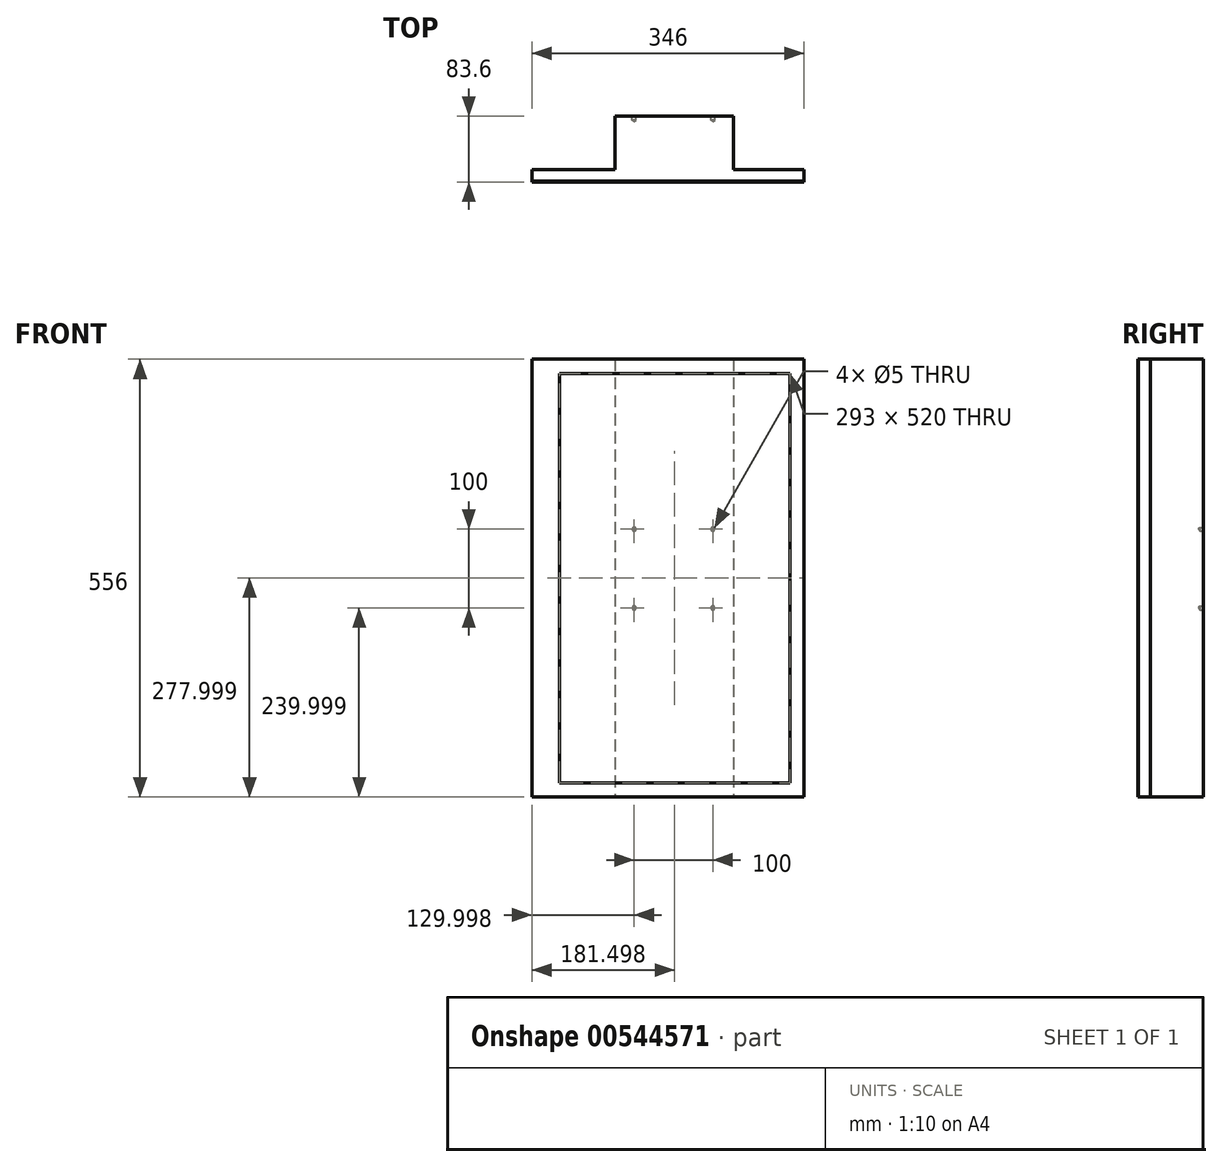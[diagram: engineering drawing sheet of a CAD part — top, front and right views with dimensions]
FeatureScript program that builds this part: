
annotation { "Feature Type Name" : "Feature", "Feature Type Description" : "" }
export const myFeature = defineFeature(function(context is Context, id is Id, definition is map)
    precondition{}
    {
        {
            assignVariable(context, id + "F0", {"name" : "mindepth", "anyValue" : 15});
        }
        {
            assignVariable(context, id + "F1", {"name" : "maxdepth", "anyValue" : 67.6});
        }
        {
            var Q0;
            Q0=qCreatedBy(makeId("Front.planeOp"),FACE);
            var sketch = newSketch(context, id + "F2", { "sketchPlane" : qUnion([Q0])});
            skLineSegment(sketch, "E0.bottom", {"start": v(-201, -247.88) * mm, "end": v(145, -247.88) * mm});
            skLineSegment(sketch, "E0.top", {"start": v(-201, 308.12) * mm, "end": v(145, 308.12) * mm});
            skLineSegment(sketch, "E0.left", {"start": v(-201, -247.88) * mm, "end": v(-201, 308.12) * mm});
            skLineSegment(sketch, "E0.right", {"start": v(145, -247.88) * mm, "end": v(145, 308.12) * mm});
            skSolve(sketch);
        }
        {
            var Q0;
            Q0=makeQuery(id+"F2.imprint","IMPRINT",FACE,{"disambiguationData":[TD([[makeQuery(id+"F2.imprint","IMPRINT",EDGE,{"derivedFrom":sQuery(id+"F2.wireOp",EDGE,"E0.bottom")}),1.0]])]});
            extrude(context, id + "F3", {"entities" : qUnion([Q0]), "oppositeDirection" : true, "depth" : (getVariable(context, 'mindepth')) * mm, "offsetDistance" : 25 * mm});
        }
        {
            var Q0;
            Q0=makeQuery(id+"F3.opExtrude","CAP_FACE",FACE,{"disambiguationData":[OSD([sQuery(id+"F2.wireOp",EDGE,"E0.bottom"),sQuery(id+"F2.wireOp",EDGE,"E0.top"),sQuery(id+"F2.wireOp",EDGE,"E0.left"),sQuery(id+"F2.wireOp",EDGE,"E0.right")])],"isStart":false});
            var sketch = newSketch(context, id + "F4", { "sketchPlane" : qUnion([Q0])});
            skLineSegment(sketch, "E1.bottom", {"start": v(-55, 308.12) * mm, "end": v(95, 308.12) * mm});
            skLineSegment(sketch, "E1.top", {"start": v(-55, -247.88) * mm, "end": v(95, -247.88) * mm});
            skLineSegment(sketch, "E1.left", {"start": v(-55, 308.12) * mm, "end": v(-55, -247.88) * mm});
            skLineSegment(sketch, "E1.right", {"start": v(95, 308.12) * mm, "end": v(95, -247.88) * mm});
            skSolve(sketch);
        }
        {
            var Q0;
            Q0=makeQuery(id+"F4.imprint","IMPRINT",FACE,{"disambiguationData":[TD([[makeQuery(id+"F4.imprint","IMPRINT",EDGE,{"derivedFrom":sQuery(id+"F4.wireOp",EDGE,"E1.bottom")}),1.0]])]});
            extrude(context, id + "F5", {"entities" : qUnion([Q0]), "operationType" : NewBodyOperationType.ADD, "depth" : (getVariable(context, 'maxdepth')) * mm, "offsetDistance" : 25 * mm});
        }
        {
            var Q0;
            Q0=makeQuery(id+"F5.opExtrude","CAP_FACE",FACE,{"disambiguationData":[OSD([sQuery(id+"F4.wireOp",EDGE,"E1.bottom"),sQuery(id+"F4.wireOp",EDGE,"E1.top"),sQuery(id+"F4.wireOp",EDGE,"E1.left"),sQuery(id+"F4.wireOp",EDGE,"E1.right")])],"isStart":false});
            var sketch = newSketch(context, id + "F6", { "sketchPlane" : qUnion([Q0])});
            skLineSegment(sketch, "E2.bottom", {"start": v(-29, 92.12) * mm, "end": v(71, 92.12) * mm, "construction": true});
            skLineSegment(sketch, "E2.top", {"start": v(-29, -7.88) * mm, "end": v(71, -7.88) * mm, "construction": true});
            skLineSegment(sketch, "E2.left", {"start": v(-29, 92.12) * mm, "end": v(-29, -7.88) * mm, "construction": true});
            skLineSegment(sketch, "E2.right", {"start": v(71, 92.12) * mm, "end": v(71, -7.88) * mm, "construction": true});
            skPoint(sketch, "E3", {"position": v(-29, 92.12) * mm});
            skPoint(sketch, "E4", {"position": v(71, 92.12) * mm});
            skPoint(sketch, "E5", {"position": v(71, -7.88) * mm});
            skPoint(sketch, "E6", {"position": v(-29, -7.88) * mm});
            skSolve(sketch);
        }
        {
            var Q0;
            Q0=sQuery(id+"F6.wireOp",VERTEX,"E3");
            var Q1;
            Q1=sQuery(id+"F6.wireOp",VERTEX,"E4");
            var Q2;
            Q2=sQuery(id+"F6.wireOp",VERTEX,"E5");
            var Q3;
            Q3=sQuery(id+"F6.wireOp",VERTEX,"E6");
            var Q4;
            Q4=makeQuery(id+"F3.opExtrude","SWEPT_BODY",BODY,{"disambiguationData":[OSD([sQuery(id+"F2.wireOp",EDGE,"E0.bottom"),sQuery(id+"F2.wireOp",EDGE,"E0.top"),sQuery(id+"F2.wireOp",EDGE,"E0.left"),sQuery(id+"F2.wireOp",EDGE,"E0.right")])]});
            hole(context, id + "F7", {"style" : HoleStyle.SIMPLE, "endStyle" : HoleEndStyle.BLIND, "holeDiameter" : 5 * mm, "holeDepth" : 5 * mm, "isTappedThrough" : true, "tappedDepth" : 12 * mm, "tapClearance" : 3, "locations" : qUnion([Q0, Q1, Q2, Q3]), "scope" : qUnion([Q4])});
        }
        {
            var Q0;
            Q0=makeQuery(id+"F3.opExtrude","CAP_FACE",FACE,{"disambiguationData":[OSD([sQuery(id+"F2.wireOp",EDGE,"E0.bottom"),sQuery(id+"F2.wireOp",EDGE,"E0.top"),sQuery(id+"F2.wireOp",EDGE,"E0.left"),sQuery(id+"F2.wireOp",EDGE,"E0.right")])],"isStart":true});
            var sketch = newSketch(context, id + "F8", { "sketchPlane" : qUnion([Q0])});
            skLineSegment(sketch, "E7.bottom", {"start": v(-166, 290.12) * mm, "end": v(127, 290.12) * mm});
            skLineSegment(sketch, "E7.top", {"start": v(-166, -229.88) * mm, "end": v(127, -229.88) * mm});
            skLineSegment(sketch, "E7.left", {"start": v(-166, 290.12) * mm, "end": v(-166, -229.88) * mm});
            skLineSegment(sketch, "E7.right", {"start": v(127, 290.12) * mm, "end": v(127, -229.88) * mm});
            skSolve(sketch);
        }
        {
            var Q0;
            Q0=makeQuery(id+"F8.imprint","IMPRINT",FACE,{"disambiguationData":[TD([[makeQuery(id+"F8.imprint","IMPRINT",EDGE,{"derivedFrom":sQuery(id+"F8.wireOp",EDGE,"E7.bottom")}),1.0]])]});
            extrude(context, id + "F9", {"entities" : qUnion([Q0]), "depth" : 1 * mm, "offsetDistance" : 25 * mm});
        }
    });
